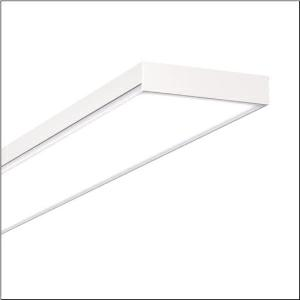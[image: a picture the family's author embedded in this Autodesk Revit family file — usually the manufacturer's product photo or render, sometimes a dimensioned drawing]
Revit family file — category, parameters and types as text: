
# Revit family: apollon_r__31_surface_51mp25wd2341w_a9bf
name_source: partatom
category: Lighting Fixtures
units: mm (PartAtom-declared; Revit-internal decimal feet)

## family parameters
Cut with Voids When Loaded = No
Host = Face
Light Source = No
Part Type = Normal
Room Calculation Point = No
Round Connector Dimension = Use Diameter
Shared = No

## types (1)
- Apollon® 31 Surface (1 x LED, 3600 lm, 28 W, 3000K)
    Apparent Load = 28 VA
    CIE Flux Codes = 61 87 97 97 100
    Color Rendering = 80
    Color Temperature = 3000K
    Default Elevation = 1800 mm
    Description = Apollon® 31 Surface, office luminaire, primary optical cover: micro prismatic cover, of PMMA, light emission: direct distribution, primary light characteristic: symmetric, installation type: surface-mounted, LED, rated luminous flux: 3.600lm, luminous efficacy: 128lm/W, light colour: 830, colour temperature: 3000K, control gear: ECG DALI, with terminal, 5-pole, mains connection: 220..240V, AC, 50/60Hz, rated input power: 28W, housing, of sheet steel, coil coated, traffic white (RAL 9016), length: 1.245mm, width: 200mm, height: 44mm, protection rating (complete): IP20, insulation class (complete): insulation class II (safety insulation), certification: CE, impact resistance: IK02, permissible operating ambient temperature: -20..+40°C, standard: EN 60598-2-22, packaging unit: 1 piece
    Height = 44 mm
    Lamp = 1 x LED
    Lamp Light Flux = 3600 lm
    Lamp Power = 28 W
    Lamp count = 1
    Length = 1245 mm
    Luminous efficacy = 129 lm/W
    Manufacturer = Siteco
    ModVariant = No
    Model = 51MP25WD2341W
    Mounting Place = Ceiling
    Mounting Type = Surface mounted
    Number of Poles = 1
    OnlyDefault = Yes
    Power Factor = 1
    Product Name = Apollon® 31 Surface
    Product group = office luminaire | ceiling mounted
    ProductGroupID = 304
    Protection Class = Protection class II
    Protection Degree = IP 20
    RLX_Detail_Level = 1
    RLX_Emergency_Light_Flux = 0 lm
    RLX_Emergency_Type = 0
    RLX_Emergency_Type_DB = No
    RlxData = <blob elided: 20745 chars, md5=d3aedf92>
    Socket = socket
    Standby Power = 0 W
    System Light Flux = 3600 lm
    System Power = 28 W
    Type Comments = Product without accessories
    Type Image = l_1007095.jpg
    URL = http://relux.com
    VarID = ---
    Voltage = 0 V
    Weight = 0.00 kg
    Width = 200 mm  [stored 0.656168 ft]

note: [stored X ft] marks values corroborated as IEEE doubles in the binary element streams (Revit-internal decimal feet)

## geometry (parser evidence)
native form markers: Blend x4, Sweep x11
no freeform markers — native parametric forms only
